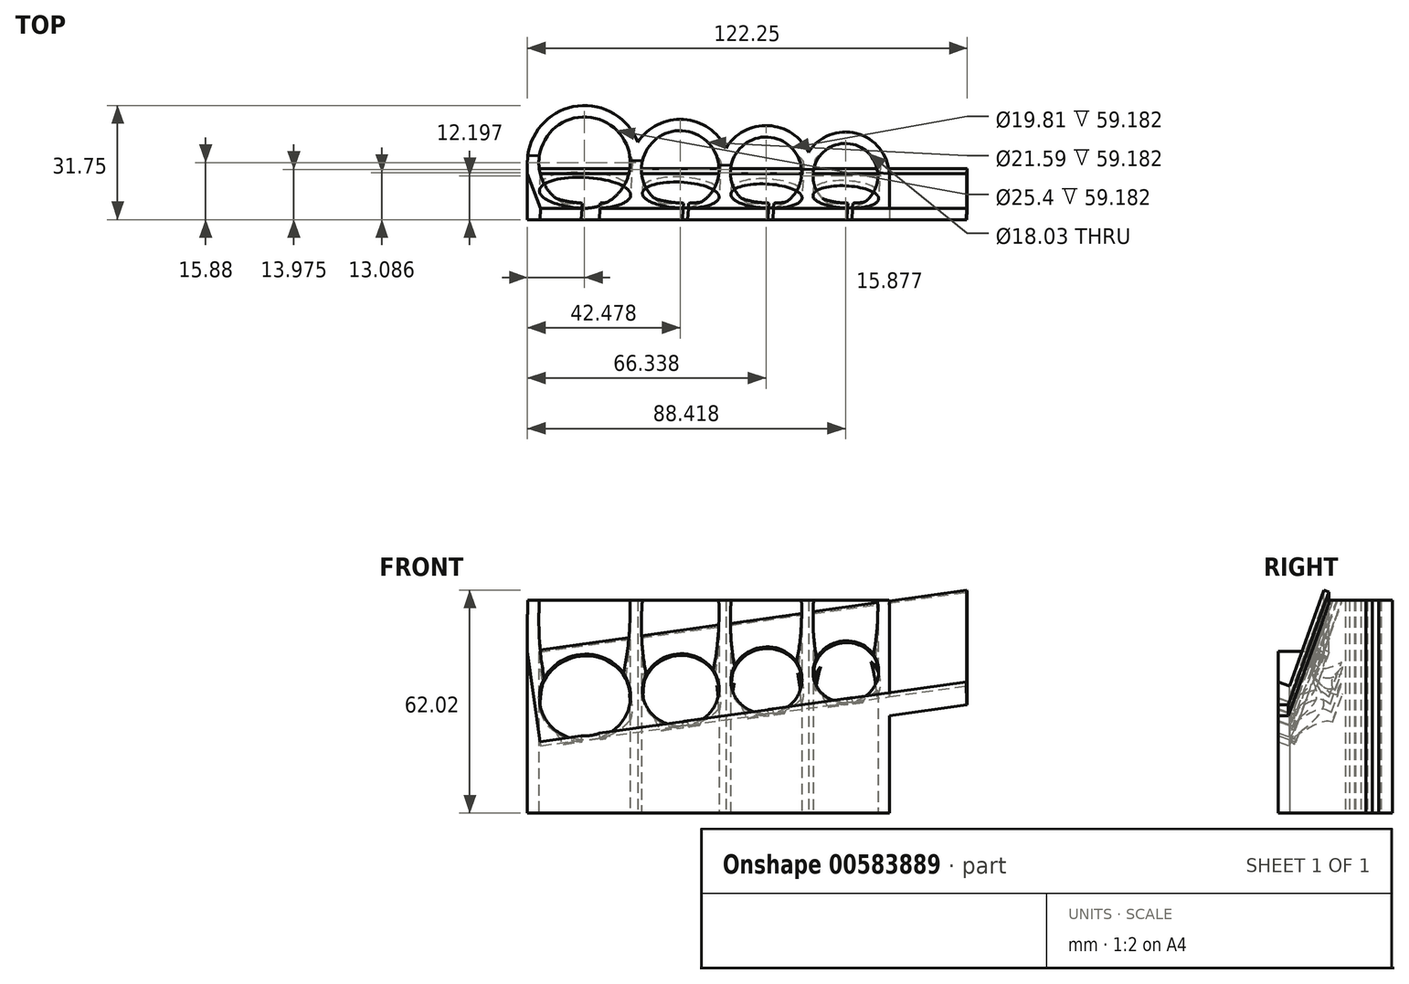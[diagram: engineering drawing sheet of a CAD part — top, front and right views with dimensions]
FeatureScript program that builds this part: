
annotation { "Feature Type Name" : "Feature", "Feature Type Description" : "" }
export const myFeature = defineFeature(function(context is Context, id is Id, definition is map)
    precondition{}
    {
        {
            var Q0;
            Q0=qCreatedBy(makeId("Top.planeOp"),FACE);
            var sketch = newSketch(context, id + "F0", { "sketchPlane" : qUnion([Q0])});
            skLineSegment(sketch, "E0", {"start": v(0, 0) * mm, "end": v(-25.73, 0) * mm, "construction": true});
            skCircle(sketch, "E1", {"center": v(-84.73, 12.7) * mm, "radius": 12.7 * mm});
            skCircle(sketch, "E2", {"center": v(-58.13, 10.8) * mm, "radius": 10.8 * mm});
            skCircle(sketch, "E3", {"center": v(-34.27, 9.9) * mm, "radius": 9.9 * mm});
            skCircle(sketch, "E4", {"center": v(-12.2, 9.02) * mm, "radius": 9.02 * mm});
            skLineSegment(sketch, "E5.top", {"start": v(-100.6, -3.18) * mm, "end": v(0, -3.18) * mm});
            skLineSegment(sketch, "E5.left", {"start": v(-100.6, 12.7) * mm, "end": v(-100.6, -3.18) * mm});
            skLineSegment(sketch, "E5.right", {"start": v(0, 28.57) * mm, "end": v(0, -3.18) * mm});
            skArc(sketch, "E6", {"start": v(-69.9, 18.33) * mm, "mid": v(-87.6, 28.31) * mm, "end": v(-100.6, 12.7) * mm});
            skArc(sketch, "E7", {"start": v(-45.46, 16.68) * mm, "mid": v(-57.19, 24.73) * mm, "end": v(-69.9, 18.33) * mm});
            skArc(sketch, "E8", {"start": v(-22.48, 15.56) * mm, "mid": v(-33.64, 22.97) * mm, "end": v(-45.46, 16.68) * mm});
            skArc(sketch, "E9", {"start": v(0, 9.02) * mm, "mid": v(-8.78, 20.72) * mm, "end": v(-22.48, 15.56) * mm});
            skLineSegment(sketch, "E10.trimOffspring", {"start": v(-34.27, 0) * mm, "end": v(-104.1, 0) * mm, "construction": true});
            skSolve(sketch);
        }
        {
            var Q0;
            Q0 = qSketchRegion(id + "F0", true);
            extrude(context, id + "F1", {"entities" : qUnion([Q0]), "depth" : 127 * mm, "offsetDistance" : 25.4 * mm});
        }
        {
            var Q0;
            Q0=makeQuery(id+"F1.opExtrude","CAP_FACE",FACE,{"disambiguationData":[OSD([sQuery(id+"F0.wireOp",EDGE,"E1"),sQuery(id+"F0.wireOp",EDGE,"E2"),sQuery(id+"F0.wireOp",EDGE,"E3"),sQuery(id+"F0.wireOp",EDGE,"E4"),sQuery(id+"F0.wireOp",EDGE,"E5.top"),sQuery(id+"F0.wireOp",EDGE,"E5.left"),sQuery(id+"F0.wireOp",EDGE,"E5.right"),sQuery(id+"F0.wireOp",EDGE,"E6"),sQuery(id+"F0.wireOp",EDGE,"E7"),sQuery(id+"F0.wireOp",EDGE,"E8"),sQuery(id+"F0.wireOp",EDGE,"E9")])],"isStart":true});
            var sketch = newSketch(context, id + "F2", { "sketchPlane" : qUnion([Q0])});
            skArc(sketch, "E11.0", {"start": v(0, -9.02) * mm, "mid": v(-8.78, -20.72) * mm, "end": v(-22.48, -15.56) * mm});
            skArc(sketch, "E11.1", {"start": v(-22.48, -15.56) * mm, "mid": v(-33.64, -22.97) * mm, "end": v(-45.46, -16.68) * mm});
            skLineSegment(sketch, "E11.2", {"start": v(-100.6, 3.18) * mm, "end": v(0, 3.18) * mm});
            skLineSegment(sketch, "E11.3", {"start": v(-100.6, -12.7) * mm, "end": v(-100.6, 3.18) * mm});
            skArc(sketch, "E11.4", {"start": v(-69.9, -18.33) * mm, "mid": v(-87.6, -28.31) * mm, "end": v(-100.6, -12.7) * mm});
            skLineSegment(sketch, "E11.5", {"start": v(0, -9.02) * mm, "end": v(0, 3.18) * mm});
            skArc(sketch, "E11.6", {"start": v(-45.46, -16.68) * mm, "mid": v(-57.19, -24.73) * mm, "end": v(-69.9, -18.33) * mm});
            skSolve(sketch);
        }
        {
            var Q0;
            Q0 = qSketchRegion(id + "F2", true);
            extrude(context, id + "F3", {"entities" : qUnion([Q0]), "operationType" : NewBodyOperationType.ADD, "depth" : 2.03 * mm, "offsetDistance" : 25.4 * mm});
        }
        {
            var Q0;
            Q0=makeQuery(id+"F1.opExtrude","CAP_EDGE",EDGE,{"disambiguationData":[OSD([sQuery(id+"F0.wireOp",EDGE,"E5.right")])],"isStart":false});
            var Q1;
            Q1=qCreatedBy(makeId("Right.planeOp"),FACE);
            cPlane(context, id + "F4", {"entities" : qUnion([Q0, Q1]), "cplaneType" : CPlaneType.LINE_ANGLE, "offset" : 25.4 * mm, "angle" : 8 * degree, "width" : 152.4 * mm, "height" : 152.4 * mm});
        }
        {
            var Q0;
            Q0=qCreatedBy(id+"F4.planeOp",FACE);
            var sketch = newSketch(context, id + "F5", { "sketchPlane" : qUnion([Q0])});
            skLineSegment(sketch, "E12", {"start": v(3.18, 100.36) * mm, "end": v(0, 99.2) * mm});
            skLineSegment(sketch, "E13", {"start": v(0, 99.2) * mm, "end": v(0, 139.77) * mm, "construction": true});
            skLineSegment(sketch, "E14", {"start": v(0, 139.77) * mm, "end": v(3.17, 139.77) * mm});
            skLineSegment(sketch, "E15", {"start": v(3.17, 139.77) * mm, "end": v(3.18, 100.36) * mm});
            skLineSegment(sketch, "E16", {"start": v(0, 99.2) * mm, "end": v(-14.76, 139.77) * mm});
            skLineSegment(sketch, "E17", {"start": v(-14.76, 139.77) * mm, "end": v(0, 139.77) * mm});
            skSolve(sketch);
        }
        {
            var Q0;
            Q0=makeQuery(id+"F5.imprint","IMPRINT",FACE,{"disambiguationData":[TD([[makeQuery(id+"F5.imprint","IMPRINT",EDGE,{"derivedFrom":sQuery(id+"F5.wireOp",EDGE,"E12")}),-1.0]])]});
            extrude(context, id + "F6", {"entities" : qUnion([Q0]), "operationType" : NewBodyOperationType.REMOVE, "depth" : 101.6 * mm, "offsetDistance" : 25.4 * mm});
        }
        {
            var Q0;
            {var subQ0=sQuery(id+"F0.wireOp",EDGE,"E5.right");var subQ1=sQuery(id+"F0.wireOp",EDGE,"E4");var subQ2=sQuery(id+"F0.wireOp",EDGE,"E9");var subQ3=makeQuery(id+"F6.opExtrude","SWEPT_FACE",FACE,{"disambiguationData":[OSD([sQuery(id+"F5.wireOp",EDGE,"E16")])]});Q0=makeQuery(id+"F6.boolean.opBoolean","COPY",FACE,{"disambiguationData":[TD([makeQuery(id+"F1.opExtrude","CAP_FACE",FACE,{"disambiguationData":[OSD([sQuery(id+"F0.wireOp",EDGE,"E1"),sQuery(id+"F0.wireOp",EDGE,"E2"),sQuery(id+"F0.wireOp",EDGE,"E3"),subQ1,sQuery(id+"F0.wireOp",EDGE,"E5.top"),sQuery(id+"F0.wireOp",EDGE,"E5.left"),subQ0,sQuery(id+"F0.wireOp",EDGE,"E6"),sQuery(id+"F0.wireOp",EDGE,"E7"),sQuery(id+"F0.wireOp",EDGE,"E8"),subQ2])],"isStart":false}),makeQuery(id+"F1.opExtrude","SWEPT_FACE",FACE,{"disambiguationData":[OSD([subQ1])]}),makeQuery(id+"F1.opExtrude","SWEPT_FACE",FACE,{"disambiguationData":[OSD([subQ0])]}),makeQuery(id+"F1.opExtrude","SWEPT_FACE",FACE,{"disambiguationData":[OSD([subQ2])]}),makeQuery(id+"F3.opExtrude","SWEPT_FACE",FACE,{"disambiguationData":[OSD([sQuery(id+"F2.wireOp",EDGE,"E11.0")])]}),makeQuery(id+"F3.opExtrude","SWEPT_FACE",FACE,{"disambiguationData":[OSD([sQuery(id+"F2.wireOp",EDGE,"E11.5")])]}),makeQuery(id+"F6.opExtrude","SWEPT_FACE",FACE,{"disambiguationData":[OSD([sQuery(id+"F5.wireOp",EDGE,"E12")])]}),subQ3])],"derivedFrom":subQ3});}
            cPlane(context, id + "F7", {"entities" : qUnion([Q0]), "cplaneType" : CPlaneType.OFFSET, "offset" : 1.52 * mm, "oppositeDirection" : true, "width" : 152.4 * mm, "height" : 152.4 * mm});
        }
        {
            var Q0;
            Q0=qCreatedBy(id+"F7.planeOp",FACE);
            var sketch = newSketch(context, id + "F8", { "sketchPlane" : qUnion([Q0])});
            skLineSegment(sketch, "E18.0", {"start": v(-95.4, 81.43) * mm, "end": v(23.2, 97.1) * mm});
            skLineSegment(sketch, "E19", {"start": v(-95.4, 81.43) * mm, "end": v(-99.08, 109.26) * mm});
            skLineSegment(sketch, "E20", {"start": v(-99.08, 109.26) * mm, "end": v(23.2, 125.41) * mm});
            skLineSegment(sketch, "E21", {"start": v(23.2, 125.41) * mm, "end": v(23.2, 97.1) * mm});
            skSolve(sketch);
        }
        {
            var Q0;
            Q0=makeQuery(id+"F8.imprint","IMPRINT",FACE,{"disambiguationData":[TD([[makeQuery(id+"F8.imprint","IMPRINT",EDGE,{"derivedFrom":sQuery(id+"F8.wireOp",EDGE,"E18.0")}),1.0]])]});
            extrude(context, id + "F9", {"entities" : qUnion([Q0]), "operationType" : NewBodyOperationType.ADD, "depth" : 1.5 * mm, "offsetDistance" : 25.4 * mm});
        }
        {
            var Q0;
            {var subQ0=sQuery(id+"F8.wireOp",EDGE,"E18.0");var subQ1=sQuery(id+"F8.wireOp",EDGE,"E20");var subQ2=sQuery(id+"F8.wireOp",EDGE,"E21");Q0=makeQuery(id+"F9.boolean.opBoolean","SPLIT",FACE,{"disambiguationData":[TD([makeQuery(id+"F1.opExtrude","SWEPT_FACE",FACE,{"disambiguationData":[OSD([sQuery(id+"F0.wireOp",EDGE,"E5.right")])]})])],"derivedFrom":makeQuery(id+"F9.opExtrude","CAP_FACE",FACE,{"disambiguationData":[OSD([subQ0,sQuery(id+"F8.wireOp",EDGE,"E19"),subQ1,subQ2])],"isStart":false})});}
            var sketch = newSketch(context, id + "F10", { "sketchPlane" : qUnion([Q0])});
            skLineSegment(sketch, "E22", {"start": v(-83.08, 138.69) * mm, "end": v(-83.08, 73.1) * mm, "construction": true});
            skLineSegment(sketch, "E23", {"start": v(-56.44, 140.53) * mm, "end": v(-56.44, 81.08) * mm, "construction": true});
            skLineSegment(sketch, "E24", {"start": v(-32.57, 144.95) * mm, "end": v(-32.57, 84.4) * mm, "construction": true});
            skLineSegment(sketch, "E25", {"start": v(-10.48, 142.25) * mm, "end": v(-10.48, 85.25) * mm, "construction": true});
            skCircle(sketch, "E26", {"center": v(-83.08, 95.62) * mm, "radius": 12.7 * mm});
            skCircle(sketch, "E27", {"center": v(-56.44, 97.32) * mm, "radius": 10.67 * mm});
            skCircle(sketch, "E28", {"center": v(-32.57, 99.7) * mm, "radius": 9.9 * mm});
            skCircle(sketch, "E29", {"center": v(-10.48, 101.85) * mm, "radius": 9.14 * mm});
            skSolve(sketch);
        }
        {
            var Q0;
            Q0 = qSketchRegion(id + "F10", true);
            extrude(context, id + "F11", {"entities" : qUnion([Q0]), "operationType" : NewBodyOperationType.REMOVE, "oppositeDirection" : true, "depth" : 10.16 * mm, "offsetDistance" : 25.4 * mm, "hasSecondDirection" : true, "secondDirectionOppositeDirection" : false, "secondDirectionDepth" : 25.4 * mm});
        }
        {
            var Q0;
            Q0=qCreatedBy(id+"F4.planeOp",FACE);
            var sketch = newSketch(context, id + "F12", { "sketchPlane" : qUnion([Q0])});
            skLineSegment(sketch, "E30", {"start": v(3.18, 100.36) * mm, "end": v(-1.43, 98.69) * mm});
            skLineSegment(sketch, "E31", {"start": v(-1.43, 98.69) * mm, "end": v(0.27, 94.01) * mm});
            skLineSegment(sketch, "E32", {"start": v(0.27, 94.01) * mm, "end": v(3.18, 94.01) * mm});
            skLineSegment(sketch, "E33", {"start": v(3.18, 94.01) * mm, "end": v(3.18, 100.36) * mm});
            skSolve(sketch);
        }
        {
            var Q0;
            Q0 = qSketchRegion(id + "F12", true);
            var Q1;
            Q1=makeQuery(id+"F9.opExtrude","SWEPT_FACE",FACE,{"disambiguationData":[OSD([sQuery(id+"F8.wireOp",EDGE,"E21")])]});
            var Q2;
            Q2=makeQuery(id+"F3.boolean.opBoolean","MERGE",FACE,{"derivedFrom":[makeQuery(id+"F1.opExtrude","SWEPT_FACE",FACE,{"disambiguationData":[OSD([sQuery(id+"F0.wireOp",EDGE,"E5.right")])]}),makeQuery(id+"F3.opExtrude","SWEPT_FACE",FACE,{"disambiguationData":[OSD([sQuery(id+"F2.wireOp",EDGE,"E11.5")])]})]});
            extrude(context, id + "F13", {"entities" : qUnion([Q0]), "operationType" : NewBodyOperationType.ADD, "endBound" : BoundingType.UP_TO_SURFACE, "oppositeDirection" : true, "depth" : 25.4 * mm, "endBoundEntityFace" : qUnion([Q1]), "offsetDistance" : 25.4 * mm, "hasSecondDirection" : true, "secondDirectionBound" : SecondDirectionBoundingType.UP_TO_SURFACE, "secondDirectionOppositeDirection" : false, "secondDirectionDepth" : 25.4 * mm, "secondDirectionBoundEntityFace" : qUnion([Q2])});
        }
        {
            var Q0;
            Q0=makeQuery(id+"F13.boolean.opBoolean","MERGE",FACE,{"derivedFrom":[makeQuery(id+"F3.boolean.opBoolean","MERGE",FACE,{"derivedFrom":[makeQuery(id+"F1.opExtrude","SWEPT_FACE",FACE,{"disambiguationData":[OSD([sQuery(id+"F0.wireOp",EDGE,"E5.top")])]}),makeQuery(id+"F3.opExtrude","SWEPT_FACE",FACE,{"disambiguationData":[OSD([sQuery(id+"F2.wireOp",EDGE,"E11.2")])]})]}),makeQuery(id+"F13.opExtrude","SWEPT_FACE",FACE,{"disambiguationData":[OSD([sQuery(id+"F12.wireOp",EDGE,"E33")])]})]});
            var sketch = newSketch(context, id + "F14", { "sketchPlane" : qUnion([Q0])});
            skLineSegment(sketch, "E34.bottom", {"start": v(-100.6, -2.03) * mm, "end": v(0, -2.03) * mm});
            skLineSegment(sketch, "E34.top", {"start": v(-100.6, 67.82) * mm, "end": v(0, 67.82) * mm});
            skLineSegment(sketch, "E34.left", {"start": v(-100.6, -2.03) * mm, "end": v(-100.6, 67.82) * mm});
            skLineSegment(sketch, "E34.right", {"start": v(0, -2.03) * mm, "end": v(0, 67.82) * mm});
            skSolve(sketch);
        }
        {
            var Q0;
            Q0 = qSketchRegion(id + "F14", true);
            extrude(context, id + "F15", {"entities" : qUnion([Q0]), "operationType" : NewBodyOperationType.REMOVE, "oppositeDirection" : true, "depth" : 50.8 * mm, "offsetDistance" : 25.4 * mm});
        }
    });
